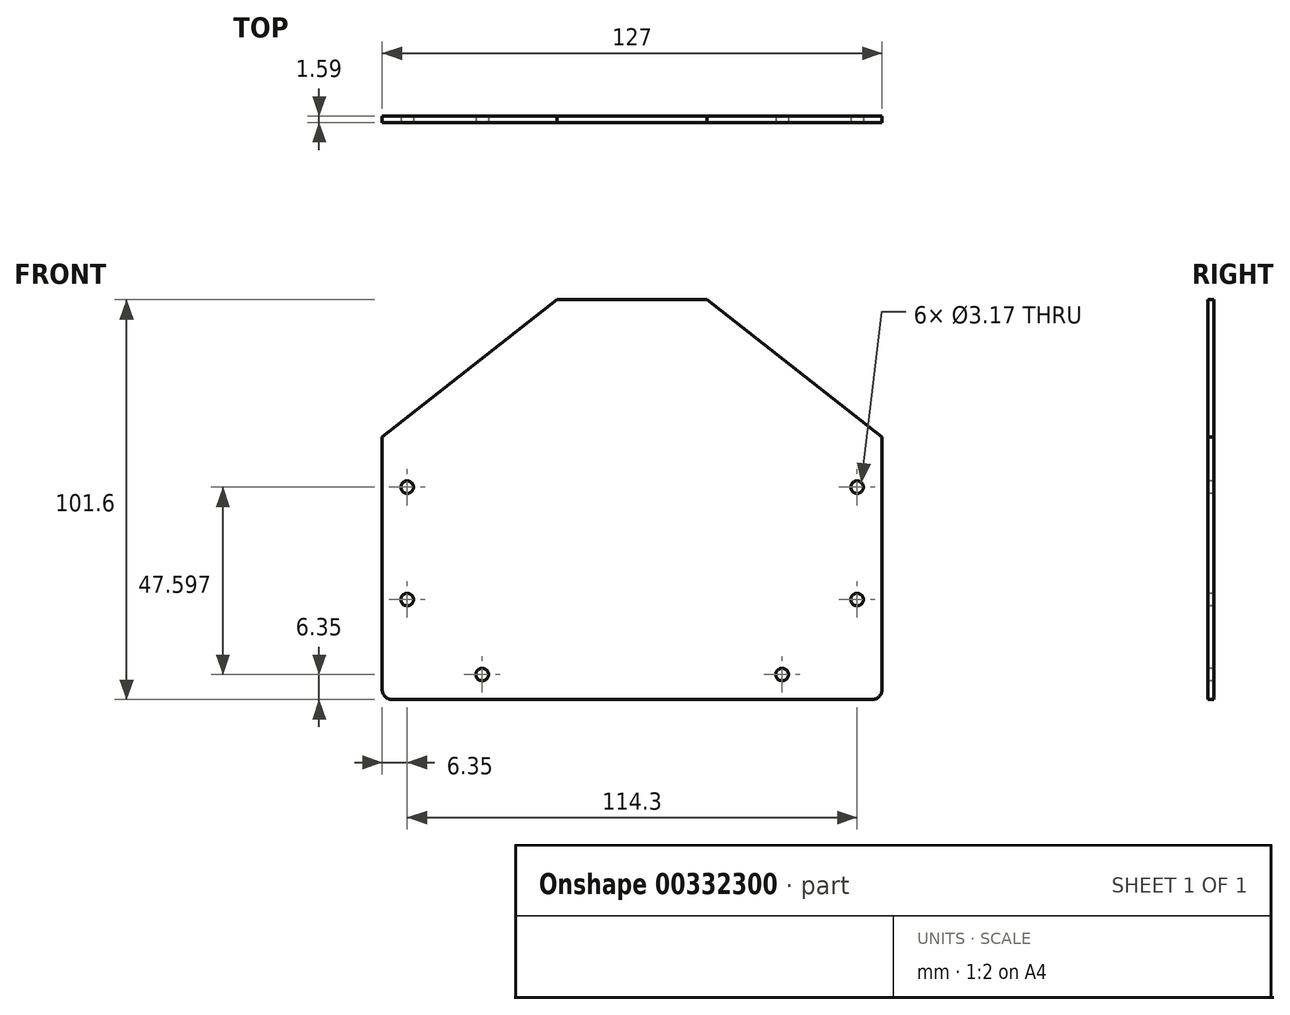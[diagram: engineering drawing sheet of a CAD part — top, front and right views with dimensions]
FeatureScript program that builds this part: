
annotation { "Feature Type Name" : "Feature", "Feature Type Description" : "" }
export const myFeature = defineFeature(function(context is Context, id is Id, definition is map)
    precondition{}
    {
        {
            var Q0;
            Q0=qCreatedBy(makeId("Front.planeOp"),FACE);
            var sketch = newSketch(context, id + "F0", { "sketchPlane" : qUnion([Q0])});
            skLineSegment(sketch, "E0.bottom", {"start": v(2.54, 0) * mm, "end": v(124.46, 0) * mm});
            skLineSegment(sketch, "E0.top", {"start": v(44.45, 101.6) * mm, "end": v(82.55, 101.6) * mm});
            skLineSegment(sketch, "E0.left", {"start": v(0, 2.54) * mm, "end": v(0, 66.68) * mm});
            skLineSegment(sketch, "E0.right", {"start": v(127, 2.54) * mm, "end": v(127, 66.68) * mm});
            skLineSegment(sketch, "E1", {"start": v(82.55, 101.6) * mm, "end": v(127, 66.68) * mm});
            skLineSegment(sketch, "E2", {"start": v(44.45, 101.6) * mm, "end": v(0, 66.68) * mm});
            skPoint(sketch, "E3.visualSharp", {"position": v(0, 0) * mm});
            skArc(sketch, "E3.filletArc", {"start": v(0, 2.54) * mm, "mid": v(0.74, 0.74) * mm, "end": v(2.54, 0) * mm});
            skPoint(sketch, "E4.visualSharp", {"position": v(127, 0) * mm});
            skArc(sketch, "E4.filletArc", {"start": v(124.46, 0) * mm, "mid": v(126.26, 0.74) * mm, "end": v(127, 2.54) * mm});
            skSolve(sketch);
        }
        {
            var Q0;
            Q0=makeQuery(id+"F0.imprint","IMPRINT",FACE,{"disambiguationData":[TD([[makeQuery(id+"F0.imprint","IMPRINT",EDGE,{"derivedFrom":sQuery(id+"F0.wireOp",EDGE,"E0.bottom")}),1.0]])]});
            extrude(context, id + "F1", {"entities" : qUnion([Q0]), "depth" : 1.59 * mm});
        }
        {
            var Q0;
            Q0=makeQuery(id+"F1.opExtrude","CAP_FACE",FACE,{"disambiguationData":[OSD([sQuery(id+"F0.wireOp",EDGE,"E0.bottom"),sQuery(id+"F0.wireOp",EDGE,"E0.top"),sQuery(id+"F0.wireOp",EDGE,"E0.left"),sQuery(id+"F0.wireOp",EDGE,"E0.right"),sQuery(id+"F0.wireOp",EDGE,"E1"),sQuery(id+"F0.wireOp",EDGE,"E2")])],"isStart":false});
            var sketch = newSketch(context, id + "F2", { "sketchPlane" : qUnion([Q0])});
            skLineSegment(sketch, "E5", {"start": v(0, 0) * mm, "end": v(6.35, 0) * mm, "construction": true});
            skLineSegment(sketch, "E6", {"start": v(6.35, 0) * mm, "end": v(6.35, 25.4) * mm, "construction": true});
            skLineSegment(sketch, "E7", {"start": v(6.35, 25.4) * mm, "end": v(6.35, 66.65) * mm, "construction": true});
            skLineSegment(sketch, "E8", {"start": v(6.35, 66.65) * mm, "end": v(6.35, 53.95) * mm, "construction": true});
            skLineSegment(sketch, "E9", {"start": v(0, 0) * mm, "end": v(0, 6.35) * mm, "construction": true});
            skLineSegment(sketch, "E10", {"start": v(0, 6.35) * mm, "end": v(25.4, 6.35) * mm, "construction": true});
            skLineSegment(sketch, "E11", {"start": v(0, 0) * mm, "end": v(127, 0) * mm, "construction": true});
            skPoint(sketch, "E11.endSnap0", {"position": v(3.18, 0) * mm});
            skLineSegment(sketch, "E12", {"start": v(63.5, 0) * mm, "end": v(63.5, 79.36) * mm, "construction": true});
            skCircle(sketch, "E13", {"center": v(6.35, 53.95) * mm, "radius": 1.59 * mm});
            skCircle(sketch, "E14", {"center": v(6.35, 25.4) * mm, "radius": 1.59 * mm});
            skCircle(sketch, "E15", {"center": v(25.4, 6.35) * mm, "radius": 1.59 * mm});
            skCircle(sketch, "E16.MirrorC", {"center": v(120.65, 53.95) * mm, "radius": 1.59 * mm});
            skCircle(sketch, "E17.MirrorC", {"center": v(120.65, 25.4) * mm, "radius": 1.59 * mm});
            skCircle(sketch, "E18.MirrorC", {"center": v(101.6, 6.35) * mm, "radius": 1.59 * mm});
            skSolve(sketch);
        }
        {
            var Q0;
            Q0=qSketchRegion(id+"F2",true);
            extrude(context, id + "F3", {"entities" : qUnion([Q0]), "operationType" : NewBodyOperationType.REMOVE, "endBound" : BoundingType.UP_TO_NEXT, "oppositeDirection" : true, "depth" : 25.4 * mm});
        }
    });
